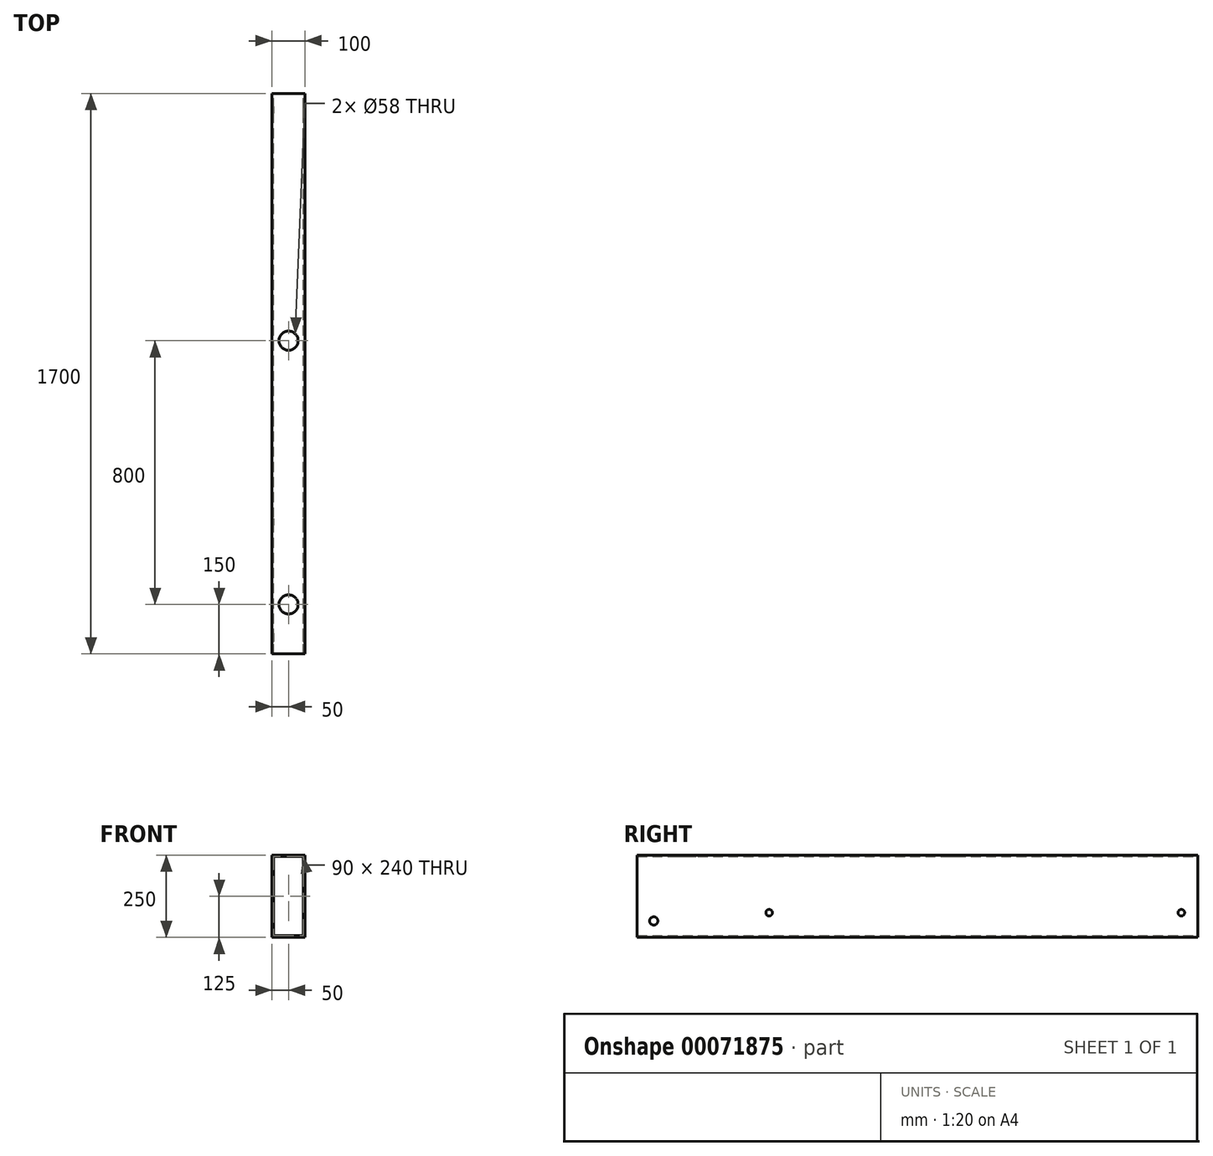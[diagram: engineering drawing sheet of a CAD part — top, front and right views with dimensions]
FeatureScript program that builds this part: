
annotation { "Feature Type Name" : "Feature", "Feature Type Description" : "" }
export const myFeature = defineFeature(function(context is Context, id is Id, definition is map)
    precondition{}
    {
        {
            var Q0;
            Q0=qCreatedBy(makeId("Front.planeOp"),FACE);
            var sketch = newSketch(context, id + "F0", { "sketchPlane" : qUnion([Q0])});
            skLineSegment(sketch, "E0.bottom", {"start": v(50, -125) * mm, "end": v(-50, -125) * mm});
            skLineSegment(sketch, "E0.top", {"start": v(50, 125) * mm, "end": v(-50, 125) * mm});
            skLineSegment(sketch, "E0.left", {"start": v(50, -125) * mm, "end": v(50, 125) * mm});
            skLineSegment(sketch, "E0.right", {"start": v(-50, -125) * mm, "end": v(-50, 125) * mm});
            skPoint(sketch, "E0.middle", {"position": v(0, 0) * mm});
            skLineSegment(sketch, "E1.bottom", {"start": v(-45, 120) * mm, "end": v(45, 120) * mm});
            skLineSegment(sketch, "E1.top", {"start": v(-45, -120) * mm, "end": v(45, -120) * mm});
            skLineSegment(sketch, "E1.left", {"start": v(-45, 120) * mm, "end": v(-45, -120) * mm});
            skLineSegment(sketch, "E1.right", {"start": v(45, 120) * mm, "end": v(45, -120) * mm});
            skSolve(sketch);
        }
        {
            var Q0;
            Q0 = qSketchRegion(id + "F0", true);
            extrude(context, id + "F1", {"entities" : qUnion([Q0]), "depth" : 1700 * mm});
        }
        {
            var Q0;
            Q0=makeQuery(id+"F1.opExtrude","SWEPT_FACE",FACE,{"disambiguationData":[OSD([sQuery(id+"F0.wireOp",EDGE,"E0.left")])]});
            var sketch = newSketch(context, id + "F2", { "sketchPlane" : qUnion([Q0])});
            skCircle(sketch, "E2", {"center": v(-1300, -50) * mm, "radius": 10 * mm});
            skSolve(sketch);
        }
        {
            var Q0;
            Q0 = qSketchRegion(id + "F2", true);
            extrude(context, id + "F3", {"entities" : qUnion([Q0]), "operationType" : NewBodyOperationType.REMOVE, "endBound" : BoundingType.THROUGH_ALL, "oppositeDirection" : true, "depth" : 25 * mm});
        }
        {
            var Q0;
            Q0=makeQuery(id+"F1.opExtrude","SWEPT_FACE",FACE,{"disambiguationData":[OSD([sQuery(id+"F0.wireOp",EDGE,"E0.left")])]});
            var sketch = newSketch(context, id + "F4", { "sketchPlane" : qUnion([Q0])});
            skCircle(sketch, "E3", {"center": v(-50, -50) * mm, "radius": 10 * mm});
            skSolve(sketch);
        }
        {
            var Q0;
            Q0 = qSketchRegion(id + "F4", true);
            extrude(context, id + "F5", {"entities" : qUnion([Q0]), "operationType" : NewBodyOperationType.REMOVE, "endBound" : BoundingType.THROUGH_ALL, "oppositeDirection" : true, "depth" : 25 * mm});
        }
        {
            var Q0;
            Q0=makeQuery(id+"F1.opExtrude","SWEPT_FACE",FACE,{"disambiguationData":[OSD([sQuery(id+"F0.wireOp",EDGE,"E0.top")])]});
            var sketch = newSketch(context, id + "F6", { "sketchPlane" : qUnion([Q0])});
            skCircle(sketch, "E4", {"center": v(0, -1550) * mm, "radius": 29 * mm});
            skSolve(sketch);
        }
        {
            var Q0;
            Q0=makeQuery(id+"F1.opExtrude","SWEPT_FACE",FACE,{"disambiguationData":[OSD([sQuery(id+"F0.wireOp",EDGE,"E0.top")])]});
            var sketch = newSketch(context, id + "F7", { "sketchPlane" : qUnion([Q0])});
            skCircle(sketch, "E5", {"center": v(0, -750) * mm, "radius": 29 * mm});
            skSolve(sketch);
        }
        {
            var Q0;
            Q0 = qSketchRegion(id + "F6", true);
            var Q1;
            Q1 = qSketchRegion(id + "F7", true);
            var Q2;
            Q2 = qSketchRegion(id + "FMOpO3zPfPI2vzJ_1", true);
            extrude(context, id + "F8", {"entities" : qUnion([Q0, Q1, Q2]), "operationType" : NewBodyOperationType.REMOVE, "endBound" : BoundingType.UP_TO_NEXT, "oppositeDirection" : true, "depth" : 25 * mm});
        }
        {
            var Q0;
            Q0=makeQuery(id+"F1.opExtrude","SWEPT_FACE",FACE,{"disambiguationData":[OSD([sQuery(id+"F0.wireOp",EDGE,"E0.left")])]});
            var sketch = newSketch(context, id + "F9", { "sketchPlane" : qUnion([Q0])});
            skCircle(sketch, "E6", {"center": v(-1650, -75) * mm, "radius": 12.5 * mm});
            skSolve(sketch);
        }
        {
            var Q0;
            Q0 = qSketchRegion(id + "F9", true);
            extrude(context, id + "F10", {"entities" : qUnion([Q0]), "operationType" : NewBodyOperationType.REMOVE, "endBound" : BoundingType.THROUGH_ALL, "oppositeDirection" : true, "depth" : 25 * mm});
        }
    });
